# Revit family: Sink-Undermount-Kitchen-KOHLER-Cairn-K-29825_1
name_source: partatom
category: Plumbing Fixtures
revit_build: Autodesk Revit 2017 (Build: 20160225_1515(x64)
units: mm (PartAtom-declared; Revit-internal decimal feet)

## family parameters
Cut with Voids When Loaded = No
Host = Face
OmniClass Number = 23.31.13.00
OmniClass Title = Sinks
Part Type = Normal
Room Calculation Point = No
Round Connector Dimension = Use Diameter
Shared = No

## types (2) — shared parameters
ADA Compliant = No
Assembly Code = D2010400
CW Connection = No
Cold Water Inlet = Cold Water Inlet
Date Modified = 02/18/2020
Default Elevation = 36"
Description = Undermount single-bowl farmhouse kitchen sink with faceted design
Drain Included = No
HW Connection = No
Height = 10 1/8"
Hot Water Inlet = Hot Water Inlet
Length = 21 3/16"
Manufacturer = KOHLER Co.
MasterFormat 1995 = 15410
MasterFormat 2004 = 22.41.16
Material = Neoroc
Product Documentation Link = https://www.us.kohler.com
Product Name = Cairn
Product Page URL = http://www.us.kohler.com
URL = https://www.us.kohler.com
Vent Connection = No
Waste Connection = Yes
Waste Water Outlet = Waste Water Outlet
WaterSense Certified = No
Width = 35 3/4"

## per-type parameters (varying)
| type | Finish | Model | Type |
| CM1 - Matte Black | Kohler-Neoroc-CM1-Matte_Black | K-29825-CM1 | 1 |
| CM4 - Matte Grey | Kohler-Neoroc-CM4-Matte_Grey | K-29825-CM4 | 2 |

## geometry (parser evidence)
native form markers: Sweep x5
no freeform markers — native parametric forms only
